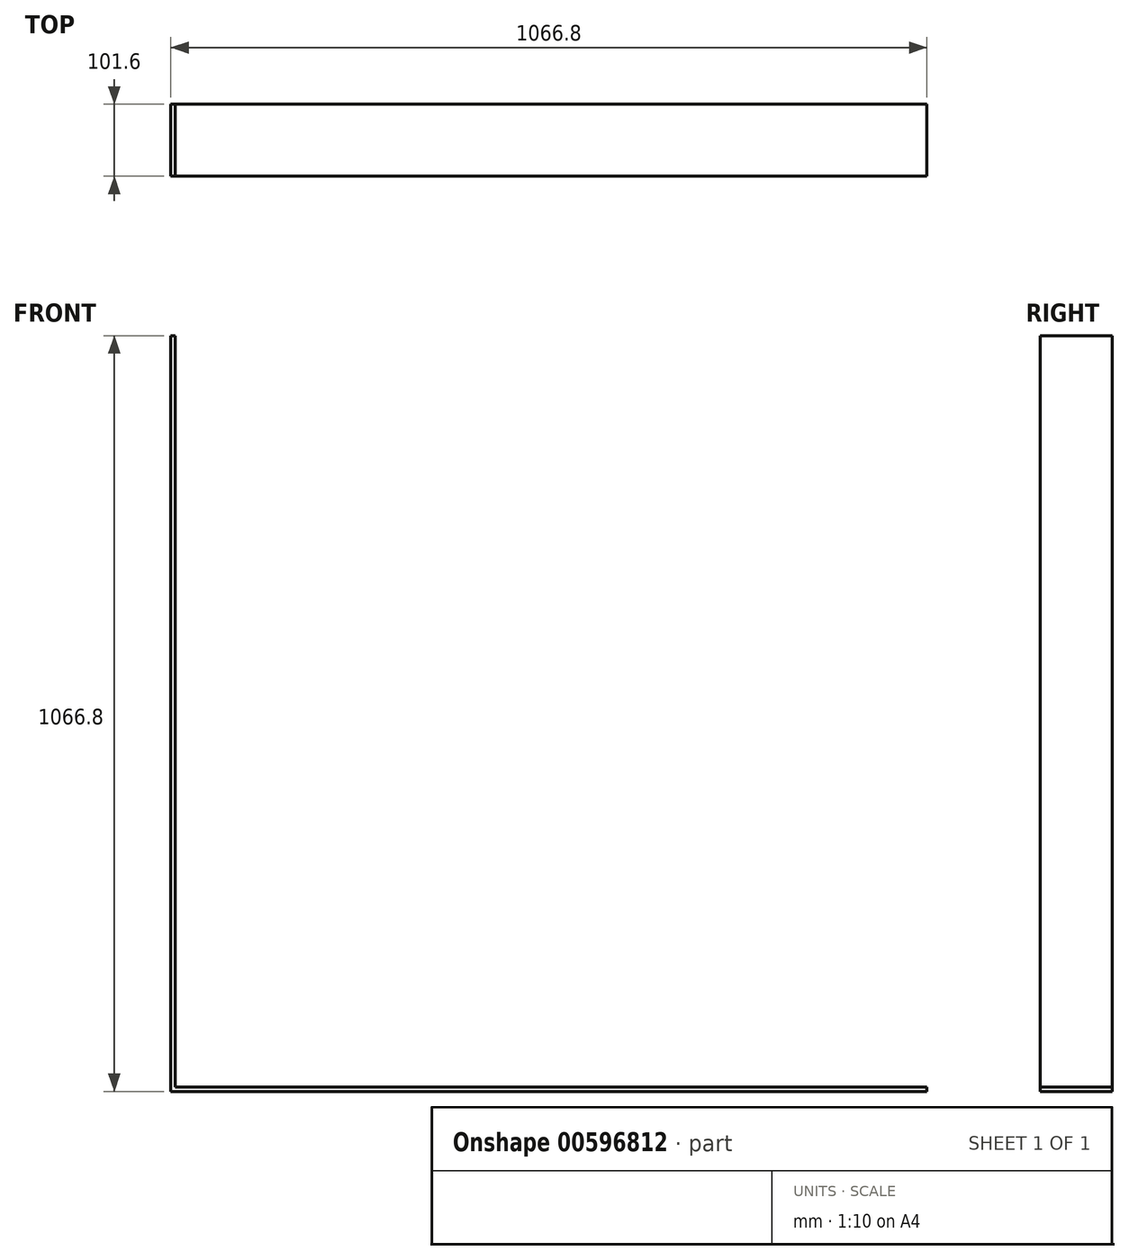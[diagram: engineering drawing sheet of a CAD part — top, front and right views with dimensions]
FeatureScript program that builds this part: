
annotation { "Feature Type Name" : "Feature", "Feature Type Description" : "" }
export const myFeature = defineFeature(function(context is Context, id is Id, definition is map)
    precondition{}
    {
        {
            var Q0;
            Q0=qCreatedBy(makeId("Front.planeOp"),FACE);
            var sketch = newSketch(context, id + "F0", { "sketchPlane" : qUnion([Q0])});
            skLineSegment(sketch, "E0.bottom", {"start": v(0, 0) * mm, "end": v(1066.8, 0) * mm});
            skLineSegment(sketch, "E0.top", {"start": v(0, 1066.8) * mm, "end": v(1066.8, 1066.8) * mm});
            skLineSegment(sketch, "E0.left", {"start": v(0, 0) * mm, "end": v(0, 1066.8) * mm});
            skLineSegment(sketch, "E0.right", {"start": v(1066.8, 0) * mm, "end": v(1066.8, 1066.8) * mm});
            skLineSegment(sketch, "E1", {"start": v(6.35, 1066.8) * mm, "end": v(6.35, 6.35) * mm});
            skLineSegment(sketch, "E2", {"start": v(6.35, 6.35) * mm, "end": v(1066.8, 6.35) * mm});
            skSolve(sketch);
        }
        {
            var Q0;
            {var subQ1=sQuery(id+"F0.wireOp",EDGE,"E0.bottom");Q0=makeQuery(id+"F0.imprint","IMPRINT",FACE,{"disambiguationData":[TD([[makeQuery(id+"F0.imprint","IMPRINT",EDGE,{"derivedFrom":subQ1}),1.0]])]});}
            extrude(context, id + "F1", {"entities" : qUnion([Q0]), "depth" : 101.6 * mm, "offsetDistance" : 25.4 * mm});
        }
    });
